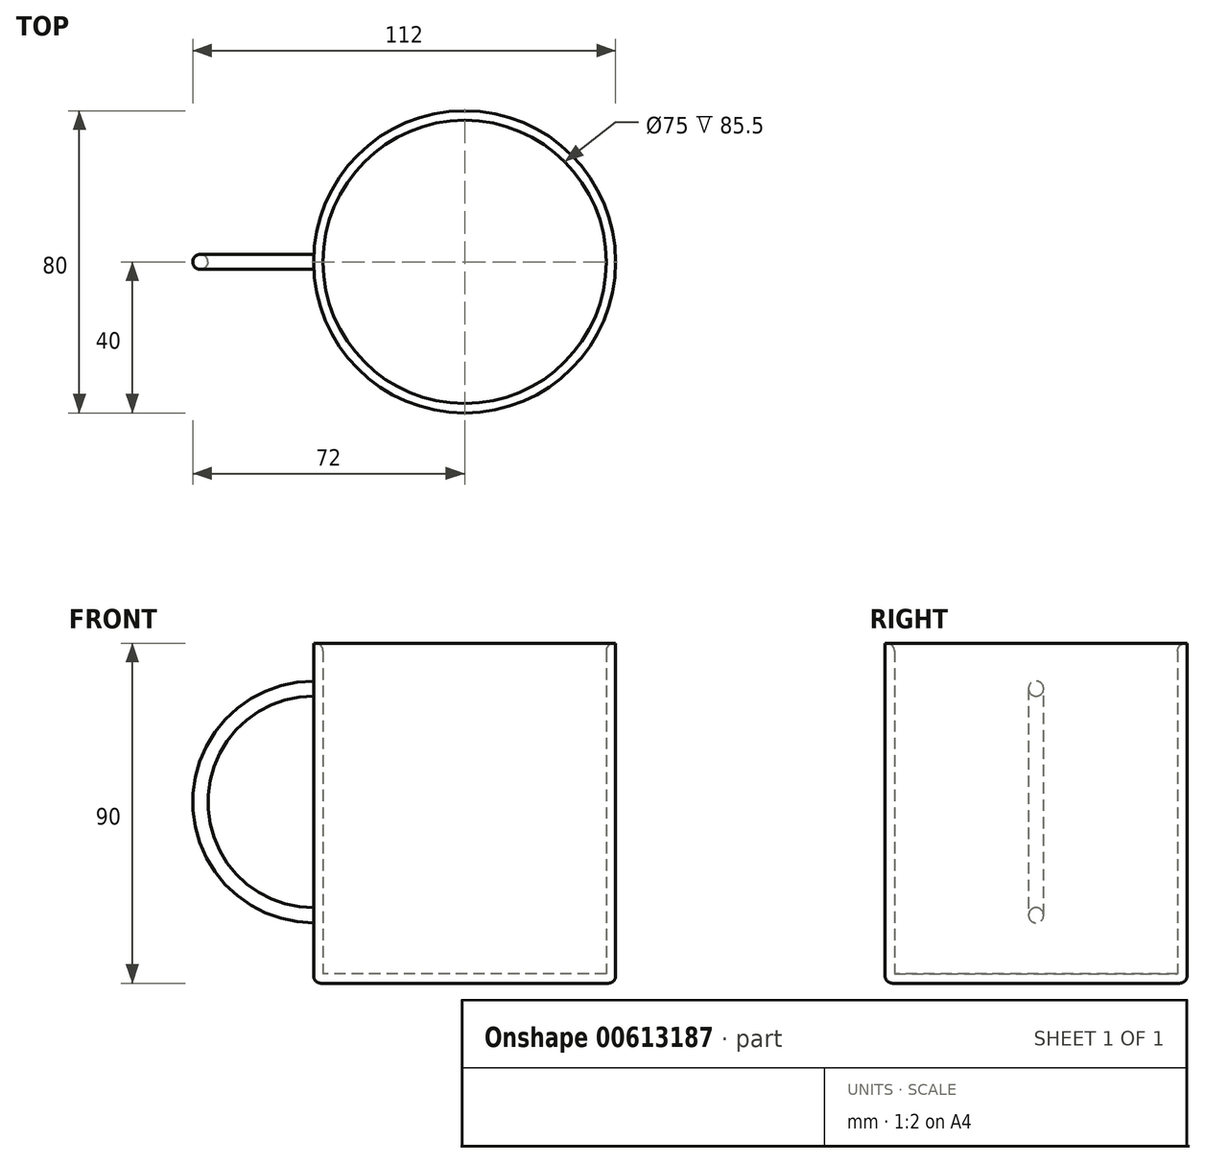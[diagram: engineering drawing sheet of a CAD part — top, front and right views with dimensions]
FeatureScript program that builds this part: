
annotation { "Feature Type Name" : "Feature", "Feature Type Description" : "" }
export const myFeature = defineFeature(function(context is Context, id is Id, definition is map)
    precondition{}
    {
        {
            var Q0;
            Q0=qCreatedBy(makeId("Top.planeOp"),FACE);
            var sketch = newSketch(context, id + "F0", { "sketchPlane" : qUnion([Q0])});
            skCircle(sketch, "E0", {"center": v(0, 0) * mm, "radius": 40 * mm});
            skSolve(sketch);
        }
        {
            var Q0;
            Q0=makeQuery(id+"F0.imprint","IMPRINT",FACE,{"disambiguationData":[TD([[makeQuery(id+"F0.imprint","IMPRINT",EDGE,{"derivedFrom":sQuery(id+"F0.wireOp",EDGE,"E0")}),1.0]])]});
            extrude(context, id + "F1", {"entities" : qUnion([Q0]), "depth" : 90 * mm, "offsetDistance" : 25 * mm});
        }
        {
            var Q0;
            Q0=makeQuery(id+"F1.opExtrude","CAP_FACE",FACE,{"disambiguationData":[OSD([sQuery(id+"F0.wireOp",EDGE,"E0")])],"isStart":false});
            shell(context, id + "F2", {"entities" : qUnion([Q0]), "thickness" : 2.5 * mm});
        }
        {
            var Q0;
            {var subQ0=sQuery(id+"F0.wireOp",EDGE,"E0");Q0=makeQuery(id+"F2.opShell","OFFSET_EDGE",EDGE,{"disambiguationData":[OSD([subQ0]),TDD([makeQuery(id+"F1.opExtrude","CAP_EDGE",EDGE,{"disambiguationData":[OSD([subQ0])],"isStart":false})])]});}
            fillet(context, id + "F3", {"entities" : qUnion([Q0]), "radius" : 2 * mm, "tangentPropagation" : true, "allowEdgeOverflow" : false});
        }
        {
            var Q0;
            Q0=qCreatedBy(makeId("Front.planeOp"),FACE);
            var sketch = newSketch(context, id + "F4", { "sketchPlane" : qUnion([Q0])});
            skLineSegment(sketch, "E1", {"start": v(-40, 0) * mm, "end": v(-40, 90) * mm});
            skLineSegment(sketch, "E2.0", {"start": v(-40, 0) * mm, "end": v(40, 0) * mm});
            skArc(sketch, "E3", {"start": v(-40, 78) * mm, "mid": v(-70, 48) * mm, "end": v(-40, 18) * mm});
            skSolve(sketch);
        }
        {
            var Q0;
            Q0=qCreatedBy(makeId("Right.planeOp"),FACE);
            cPlane(context, id + "F5", {"entities" : qUnion([Q0]), "cplaneType" : CPlaneType.OFFSET, "offset" : 40 * mm, "oppositeDirection" : true, "width" : 150 * mm, "height" : 150 * mm});
        }
        {
            var Q0;
            Q0=qCreatedBy(id+"F5.planeOp",FACE);
            var sketch = newSketch(context, id + "F6", { "sketchPlane" : qUnion([Q0])});
            skPoint(sketch, "E4.0", {"position": v(0, 78) * mm});
            skCircle(sketch, "E5", {"center": v(0, 78) * mm, "radius": 2 * mm});
            skSolve(sketch);
        }
        {
            var Q0;
            Q0=makeQuery(id+"F6.imprint","IMPRINT",FACE,{"disambiguationData":[TD([[makeQuery(id+"F6.imprint","IMPRINT",EDGE,{"derivedFrom":sQuery(id+"F6.wireOp",EDGE,"E5")}),1.0]])]});
            var Q1;
            Q1=sQuery(id+"F4.wireOp",EDGE,"E3");
            sweep(context, id + "F7", {"operationType" : NewBodyOperationType.ADD, "profiles" : qUnion([Q0]), "path" : qUnion([Q1])});
        }
        {
            var Q0;
            Q0=makeQuery(id+"F1.opExtrude","CAP_EDGE",EDGE,{"disambiguationData":[OSD([sQuery(id+"F0.wireOp",EDGE,"E0")])],"isStart":true});
            fillet(context, id + "F8", {"entities" : qUnion([Q0]), "radius" : 2 * mm, "tangentPropagation" : true, "allowEdgeOverflow" : false});
        }
    });
